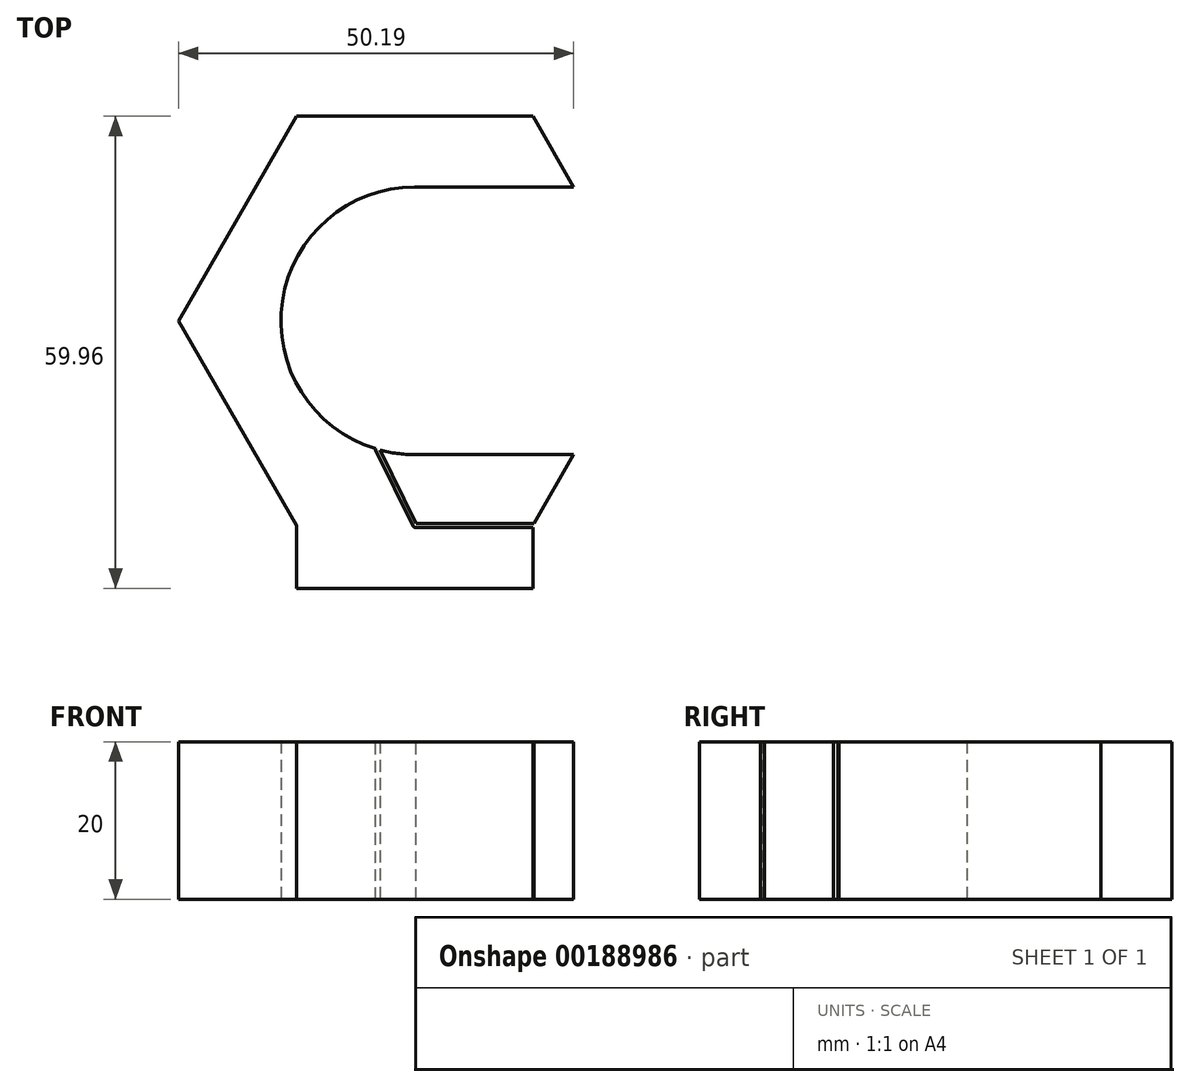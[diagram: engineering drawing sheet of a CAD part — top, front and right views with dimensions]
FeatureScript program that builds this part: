
annotation { "Feature Type Name" : "Feature", "Feature Type Description" : "" }
export const myFeature = defineFeature(function(context is Context, id is Id, definition is map)
    precondition{}
    {
        {
            var Q0;
            Q0=qCreatedBy(makeId("Top.planeOp"),FACE);
            var sketch = newSketch(context, id + "F0", { "sketchPlane" : qUnion([Q0])});
            skCircle(sketch, "E0.cCircle", {"center": v(0, 0) * mm, "radius": 25.98 * mm, "construction": true});
            skLineSegment(sketch, "E0.0", {"start": v(-15, 25.98) * mm, "end": v(15, 25.98) * mm});
            skLineSegment(sketch, "E0.1", {"start": v(15, 25.98) * mm, "end": v(20.19, 17) * mm});
            skLineSegment(sketch, "E0.2", {"start": v(20.19, -17) * mm, "end": v(15, -25.98) * mm});
            skLineSegment(sketch, "E0.4", {"start": v(-15, -25.98) * mm, "end": v(-30, 0) * mm});
            skLineSegment(sketch, "E0.5", {"start": v(-30, 0) * mm, "end": v(-15, 25.98) * mm});
            skPoint(sketch, "E0.0.midPoint", {"position": v(0, 25.98) * mm});
            skArc(sketch, "E1", {"start": v(0, 17) * mm, "mid": v(-17, 0) * mm, "end": v(0, -17) * mm});
            skLineSegment(sketch, "E2", {"start": v(0, 17) * mm, "end": v(20.19, 17) * mm});
            skLineSegment(sketch, "E3", {"start": v(0, -17) * mm, "end": v(20.19, -17) * mm});
            skPoint(sketch, "E4.orphan", {"position": v(30, 0) * mm});
            skLineSegment(sketch, "E5", {"start": v(-15, -33.98) * mm, "end": v(15, -33.98) * mm});
            skLineSegment(sketch, "E6", {"start": v(-15, -25.98) * mm, "end": v(-15, -33.98) * mm});
            skLineSegment(sketch, "E7", {"start": v(15, -25.98) * mm, "end": v(15, -33.98) * mm});
            skSolve(sketch);
        }
        {
            var Q0;
            Q0 = qSketchRegion(id + "F0", true);
            extrude(context, id + "F1", {"entities" : qUnion([Q0]), "depth" : 20 * mm});
        }
        {
            var Q0;
            Q0=makeQuery(id+"F1.opExtrude","CAP_FACE",FACE,{"disambiguationData":[OSD([sQuery(id+"F0.wireOp",EDGE,"E0.0"),sQuery(id+"F0.wireOp",EDGE,"E0.1"),sQuery(id+"F0.wireOp",EDGE,"E0.2"),sQuery(id+"F0.wireOp",EDGE,"E0.4"),sQuery(id+"F0.wireOp",EDGE,"E0.5"),sQuery(id+"F0.wireOp",EDGE,"E1"),sQuery(id+"F0.wireOp",EDGE,"E2"),sQuery(id+"F0.wireOp",EDGE,"E3"),sQuery(id+"F0.wireOp",EDGE,"E5"),sQuery(id+"F0.wireOp",EDGE,"E6"),sQuery(id+"F0.wireOp",EDGE,"E7")])],"isStart":false});
            var sketch = newSketch(context, id + "F2", { "sketchPlane" : qUnion([Q0])});
            skLineSegment(sketch, "E8", {"start": v(15, -25.98) * mm, "end": v(0, -25.98) * mm});
            skLineSegment(sketch, "E9", {"start": v(0, -25.98) * mm, "end": v(-4.76, -16.32) * mm});
            skArc(sketch, "E10.0.startCap", {"start": v(15, -25.73) * mm, "mid": v(15.25, -25.98) * mm, "end": v(15, -26.23) * mm});
            skArc(sketch, "E10.0.endCap", {"start": v(0, -26.23) * mm, "mid": v(-0.25, -25.98) * mm, "end": v(0, -25.73) * mm});
            skLineSegment(sketch, "E10.0.left", {"start": v(15, -26.23) * mm, "end": v(0, -26.23) * mm});
            skLineSegment(sketch, "E10.0.right", {"start": v(15, -25.73) * mm, "end": v(0, -25.73) * mm});
            skArc(sketch, "E10.1.startCap", {"start": v(0.22, -25.87) * mm, "mid": v(0.11, -26.2) * mm, "end": v(-0.22, -26.1) * mm});
            skArc(sketch, "E10.1.endCap", {"start": v(-4.98, -16.43) * mm, "mid": v(-4.87, -16.1) * mm, "end": v(-4.53, -16.21) * mm});
            skLineSegment(sketch, "E10.1.left", {"start": v(-0.22, -26.1) * mm, "end": v(-4.98, -16.43) * mm});
            skLineSegment(sketch, "E10.1.right", {"start": v(0.22, -25.87) * mm, "end": v(-4.53, -16.21) * mm});
            skSolve(sketch);
        }
        {
            var Q0;
            Q0 = qSketchRegion(id + "F2", true);
            extrude(context, id + "F3", {"entities" : qUnion([Q0]), "operationType" : NewBodyOperationType.REMOVE, "oppositeDirection" : true, "depth" : 25 * mm});
        }
    });
